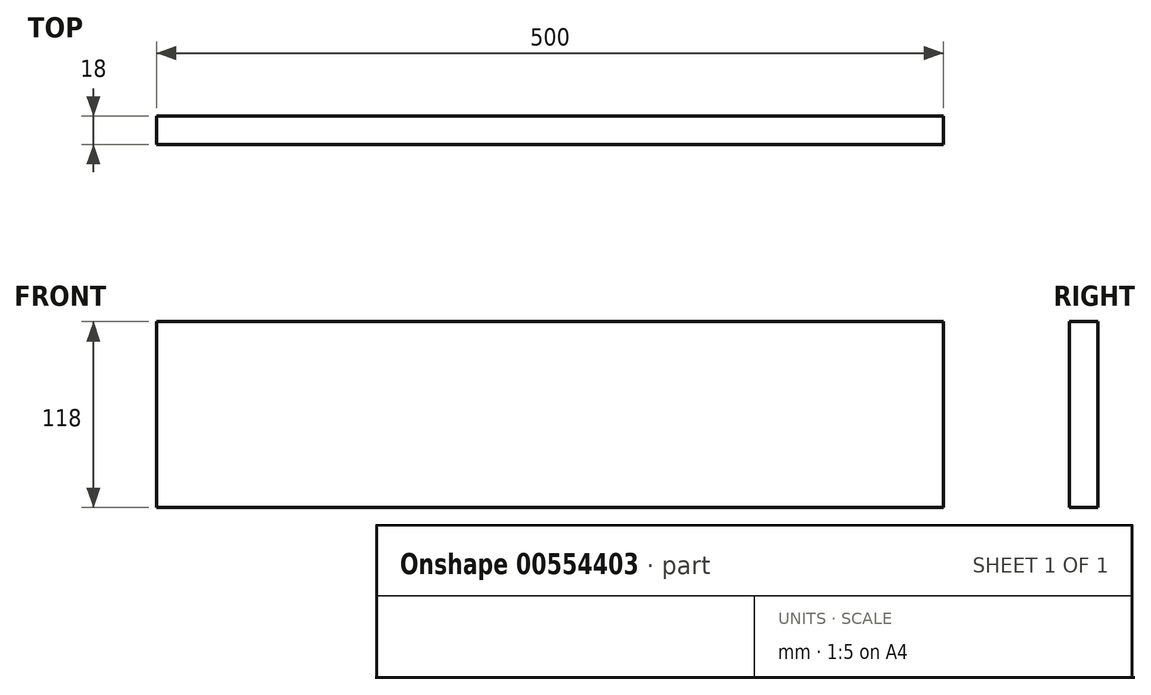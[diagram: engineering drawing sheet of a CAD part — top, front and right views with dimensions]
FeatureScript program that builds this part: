
annotation { "Feature Type Name" : "Feature", "Feature Type Description" : "" }
export const myFeature = defineFeature(function(context is Context, id is Id, definition is map)
    precondition{}
    {
        {
            var Q0;
            Q0=qCreatedBy(makeId("Front.planeOp"),FACE);
            var sketch = newSketch(context, id + "F0", { "sketchPlane" : qUnion([Q0])});
            skLineSegment(sketch, "E0.bottom", {"start": v(0, 0) * mm, "end": v(500, 0) * mm});
            skLineSegment(sketch, "E0.top", {"start": v(0, 118) * mm, "end": v(500, 118) * mm});
            skLineSegment(sketch, "E0.left", {"start": v(0, 0) * mm, "end": v(0, 118) * mm});
            skLineSegment(sketch, "E0.right", {"start": v(500, 0) * mm, "end": v(500, 118) * mm});
            skSolve(sketch);
        }
        {
            var Q0;
            Q0=makeQuery(id+"F0.imprint","IMPRINT",FACE,{"disambiguationData":[TD([[makeQuery(id+"F0.imprint","IMPRINT",EDGE,{"derivedFrom":sQuery(id+"F0.wireOp",EDGE,"E0.bottom")}),1.0]])]});
            extrude(context, id + "F1", {"entities" : qUnion([Q0]), "depth" : 18 * mm, "offsetDistance" : 25 * mm});
        }
    });
